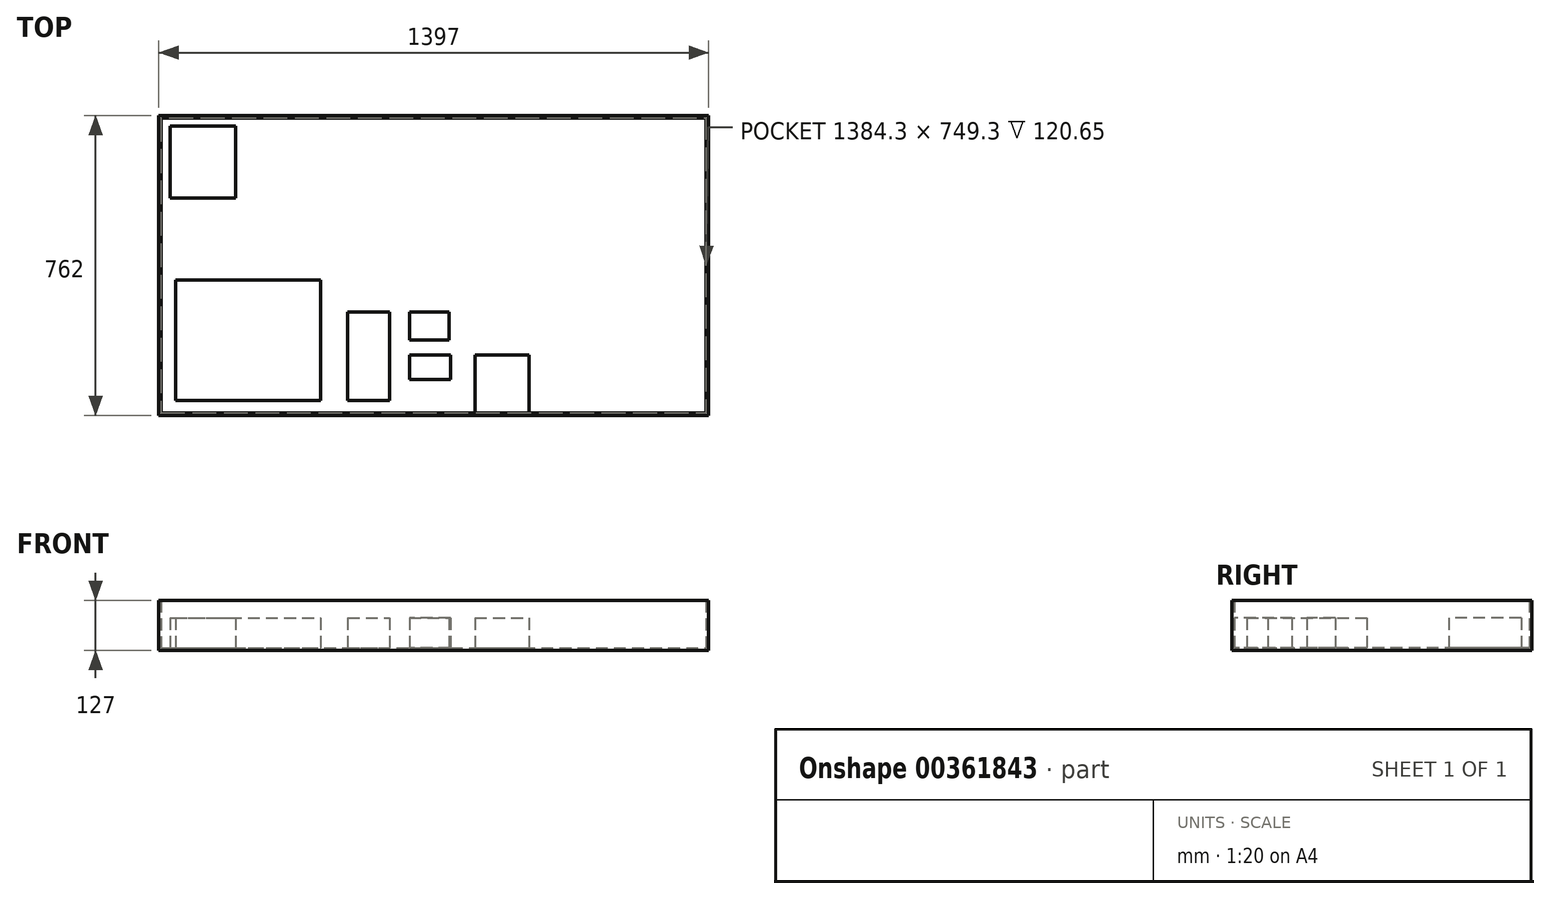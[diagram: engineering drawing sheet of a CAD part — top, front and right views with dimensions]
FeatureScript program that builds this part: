
annotation { "Feature Type Name" : "Feature", "Feature Type Description" : "" }
export const myFeature = defineFeature(function(context is Context, id is Id, definition is map)
    precondition{}
    {
        {
            var Q0;
            Q0=qCreatedBy(makeId("Top.planeOp"),FACE);
            var sketch = newSketch(context, id + "F0", { "sketchPlane" : qUnion([Q0])});
            skLineSegment(sketch, "E0.bottom", {"start": v(-698.5, 381) * mm, "end": v(698.5, 381) * mm});
            skLineSegment(sketch, "E0.top", {"start": v(-698.5, -381) * mm, "end": v(698.5, -381) * mm});
            skLineSegment(sketch, "E0.left", {"start": v(-698.5, 381) * mm, "end": v(-698.5, -381) * mm});
            skLineSegment(sketch, "E0.right", {"start": v(698.5, 381) * mm, "end": v(698.5, -381) * mm});
            skPoint(sketch, "E0.middle", {"position": v(0, 0) * mm});
            skSolve(sketch);
        }
        {
            var Q0;
            Q0 = qSketchRegion(id + "F0", true);
            extrude(context, id + "F1", {"entities" : qUnion([Q0]), "depth" : 127 * mm});
        }
        {
            var Q0;
            Q0=makeQuery(id+"F1.opExtrude","CAP_FACE",FACE,{"disambiguationData":[OSD([sQuery(id+"F0.wireOp",EDGE,"E0.bottom"),sQuery(id+"F0.wireOp",EDGE,"E0.top"),sQuery(id+"F0.wireOp",EDGE,"E0.left"),sQuery(id+"F0.wireOp",EDGE,"E0.right")])],"isStart":false});
            shell(context, id + "F2", {"entities" : qUnion([Q0]), "thickness" : 6.35 * mm});
        }
        {
            var Q0;
            Q0=makeQuery(id+"F2.opShell","OFFSET_FACE",FACE,{"disambiguationData":[OSD([sQuery(id+"F0.wireOp",EDGE,"E0.bottom"),sQuery(id+"F0.wireOp",EDGE,"E0.top"),sQuery(id+"F0.wireOp",EDGE,"E0.left"),sQuery(id+"F0.wireOp",EDGE,"E0.right")])]});
            var sketch = newSketch(context, id + "F3", { "sketchPlane" : qUnion([Q0])});
            skLineSegment(sketch, "E1.bottom", {"start": v(-656.13, -342.67) * mm, "end": v(-286.84, -342.67) * mm});
            skLineSegment(sketch, "E1.top", {"start": v(-656.13, -36.93) * mm, "end": v(-286.84, -36.93) * mm});
            skLineSegment(sketch, "E1.left", {"start": v(-656.13, -342.67) * mm, "end": v(-656.13, -36.93) * mm});
            skLineSegment(sketch, "E1.right", {"start": v(-286.84, -342.67) * mm, "end": v(-286.84, -36.93) * mm});
            skLineSegment(sketch, "E2.bottom", {"start": v(-218.14, -342.67) * mm, "end": v(-111.65, -342.67) * mm});
            skLineSegment(sketch, "E2.top", {"start": v(-218.14, -117.66) * mm, "end": v(-111.65, -117.66) * mm});
            skLineSegment(sketch, "E2.left", {"start": v(-218.14, -342.67) * mm, "end": v(-218.14, -117.66) * mm});
            skLineSegment(sketch, "E2.right", {"start": v(-111.65, -342.67) * mm, "end": v(-111.65, -117.66) * mm});
            skLineSegment(sketch, "E3.bottom", {"start": v(-61.83, -117.66) * mm, "end": v(39.5, -117.66) * mm});
            skLineSegment(sketch, "E3.top", {"start": v(-61.83, -189.8) * mm, "end": v(39.5, -189.8) * mm});
            skLineSegment(sketch, "E3.left", {"start": v(-61.83, -117.66) * mm, "end": v(-61.83, -189.8) * mm});
            skLineSegment(sketch, "E3.right", {"start": v(39.5, -117.66) * mm, "end": v(39.5, -189.8) * mm});
            skLineSegment(sketch, "E4.bottom", {"start": v(42.94, -227.59) * mm, "end": v(-61.83, -227.59) * mm});
            skLineSegment(sketch, "E4.top", {"start": v(42.94, -289.42) * mm, "end": v(-61.83, -289.42) * mm});
            skLineSegment(sketch, "E4.left", {"start": v(42.94, -227.59) * mm, "end": v(42.94, -289.42) * mm});
            skLineSegment(sketch, "E4.right", {"start": v(-61.83, -227.59) * mm, "end": v(-61.83, -289.42) * mm});
            skLineSegment(sketch, "E5.bottom", {"start": v(-669.87, 354.69) * mm, "end": v(-503.26, 354.69) * mm});
            skLineSegment(sketch, "E5.top", {"start": v(-669.87, 170.9) * mm, "end": v(-503.26, 170.9) * mm});
            skLineSegment(sketch, "E5.left", {"start": v(-669.87, 354.69) * mm, "end": v(-669.87, 170.9) * mm});
            skLineSegment(sketch, "E5.right", {"start": v(-503.26, 354.69) * mm, "end": v(-503.26, 170.9) * mm});
            skLineSegment(sketch, "E6.bottom", {"start": v(104.77, -227.59) * mm, "end": v(242.18, -227.59) * mm});
            skLineSegment(sketch, "E6.top", {"start": v(104.77, -374.65) * mm, "end": v(242.18, -374.65) * mm});
            skLineSegment(sketch, "E6.left", {"start": v(104.77, -227.59) * mm, "end": v(104.77, -374.65) * mm});
            skLineSegment(sketch, "E6.right", {"start": v(242.18, -227.59) * mm, "end": v(242.18, -374.65) * mm});
            skSolve(sketch);
        }
        {
            var Q0;
            Q0 = qSketchRegion(id + "F3", true);
            extrude(context, id + "F4", {"entities" : qUnion([Q0]), "depth" : 76.2 * mm});
        }
    });
